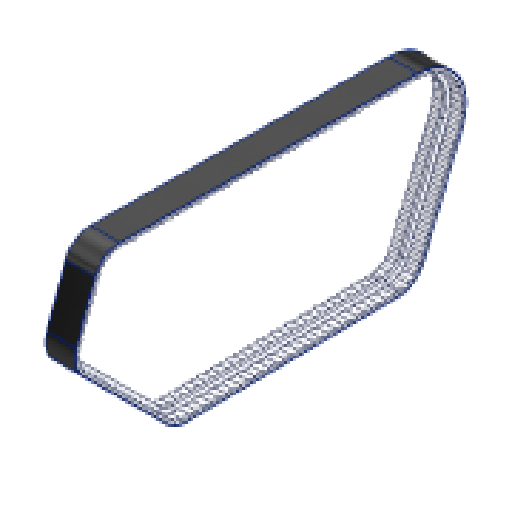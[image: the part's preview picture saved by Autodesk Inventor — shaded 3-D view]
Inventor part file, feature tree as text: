
AUTODESK INVENTOR PART (.ipt)
format: ipt  version: 2025 (Build 290162000, 162)  size: 1,061,376 bytes
history: native  units: mm
features: sketch x4, extrude x3, other x3, chamfer x2, thicken_offset x2, projected_geometry x2, plane x1, pattern_linear x1, reference x1
ambient origin geometry x8: Origin, YZ Plane, XZ Plane, XY Plane, X Axis, Y Axis, Z Axis, Center Point
bodies: Solid1 (feature_tree), Solid3 (feature_tree)
feature tree (19):
  extrude  "Extrusion1"  Depth=160.409901mm
  plane  "Work Plane1"
  extrude  "Extrusion2"  Depth=50.8mm TaperAngle=0.0deg
  chamfer  "Chamfer1"  Distance=10.0mm
  chamfer  "Chamfer2"  Distance=2.0mm Angle=45.0deg
  extrude  "Extrusion3"  Depth=10.0mm TaperAngle=0.0deg
  pattern_linear  "Rectangular Pattern1"  Count1=134 Spacing1=12.7mm
  thicken_offset  "Thicken1"
  thicken_offset  "Thicken2"
  sketch  "Sketch1"  dims[d0=79.50708mm d1=160.409901mm]
  reference  "Reference5"
  sketch  "Sketch2"  dims[d2=10.0mm d3=50.8mm d4=0.0mm d5=10.0mm d6=0.0mm d7=8.0mm d8=2.0mm d9=45.0deg]
  projected_geometry  "Projected Loop1"
  sketch  "Sketch3"  dims[d10=8.0mm d11=2.0mm d12=45.0deg d13=10.0mm d14=0.0mm d15=1340.0mm d17=12.7mm d18=6.0mm]
  projected_geometry  "Projected Loop2"
  sketch  "Sketch5"  dims[d19=6.0mm d20=2.0mm d21=2.0mm]
  other  "<userpath>\Desktop\puppycat\woodhouseMK1.iam"
  other  "woodhouseMK1.iam"
  other  "hoverboard_motor_assembly:1"
